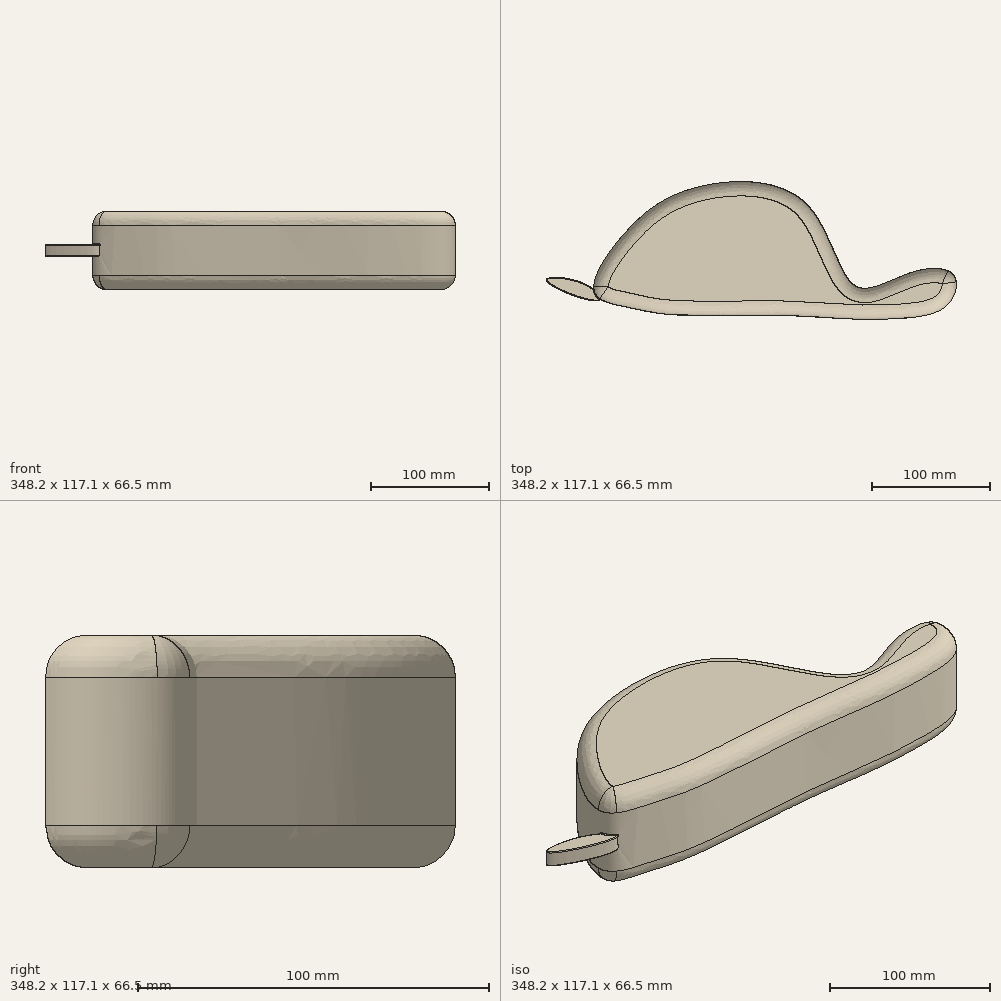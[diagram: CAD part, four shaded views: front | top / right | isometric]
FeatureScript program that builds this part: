
annotation { "Feature Type Name" : "Feature", "Feature Type Description" : "" }
export const myFeature = defineFeature(function(context is Context, id is Id, definition is map)
    precondition{}
    {
        {
            var Q0;
            Q0=qCreatedBy(makeId("Top.planeOp"),FACE);
            var sketch = newSketch(context, id + "F0", { "sketchPlane" : qUnion([Q0])});
            skFitSpline(sketch, "E0", {"points": [v(-149.95, -51.7) * mm, v(-123, 0) * mm, v(-63.14, 37.56) * mm, v(29.4, 23.95) * mm, v(71.85, -46.26) * mm, v(119.74, -34.56) * mm, v(155.12, -37.28) * mm, v(151.04, -61.23) * mm, v(114.84, -73.48) * mm, v(60.96, -74.02) * mm, v(8.98, -71.03) * mm, v(-86.54, -70.48) * mm, v(-122.46, -64.23) * mm, v(-149.95, -51.7) * mm]});
            skSolve(sketch);
        }
        {
            var Q0;
            Q0=makeQuery(id+"F0.imprint","IMPRINT",FACE,{"disambiguationData":[TD([[makeQuery(id+"F0.imprint","IMPRINT",EDGE,{"derivedFrom":sQuery(id+"F0.wireOp",EDGE,"E0")}),-1.0]])]});
            extrude(context, id + "F1", {"entities" : qUnion([Q0]), "depth" : 33.27 * mm});
        }
        {
            var Q0;
            Q0=makeQuery(id+"F1.opExtrude","CAP_FACE",FACE,{"disambiguationData":[OSD([sQuery(id+"F0.wireOp",EDGE,"E0")])],"isStart":true});
            extrude(context, id + "F2", {"entities" : qUnion([Q0]), "operationType" : NewBodyOperationType.ADD, "depth" : 33.27 * mm});
        }
        {
            var Q0;
            Q0=makeQuery(id+"F2.opExtrude","CAP_FACE",FACE,{"disambiguationData":[OSD([sQuery(id+"F0.wireOp",EDGE,"E0")])],"isStart":false});
            fillet(context, id + "F3", {"entities" : qUnion([Q0]), "radius" : 12.26 * mm, "tangentPropagation" : true, "allowEdgeOverflow" : false});
        }
        {
            var Q0;
            Q0=makeQuery(id+"F1.opExtrude","CAP_FACE",FACE,{"disambiguationData":[OSD([sQuery(id+"F0.wireOp",EDGE,"E0")])],"isStart":false});
            fillet(context, id + "F4", {"entities" : qUnion([Q0]), "radius" : 12.2 * mm, "tangentPropagation" : true, "allowEdgeOverflow" : false});
        }
        {
            var Q0;
            Q0=qCreatedBy(makeId("Top.planeOp"),FACE);
            var sketch = newSketch(context, id + "F5", { "sketchPlane" : qUnion([Q0])});
            skFitSpline(sketch, "E1", {"points": [v(-144.37, -57.1) * mm, v(-160.78, -56.76) * mm, v(-190.87, -41.03) * mm, v(-162.49, -42.74) * mm, v(-144.37, -57.1) * mm]});
            skSolve(sketch);
        }
        {
            var Q0;
            Q0=makeQuery(id+"F5.imprint","IMPRINT",FACE,{"disambiguationData":[TD([[makeQuery(id+"F5.imprint","IMPRINT",EDGE,{"derivedFrom":sQuery(id+"F5.wireOp",EDGE,"E1")}),-1.0]])]});
            extrude(context, id + "F6", {"entities" : qUnion([Q0]), "operationType" : NewBodyOperationType.ADD, "depth" : 5.08 * mm});
        }
        {
            var Q0;
            Q0=makeQuery(id+"F6.opExtrude","CAP_FACE",FACE,{"disambiguationData":[OSD([sQuery(id+"F5.wireOp",EDGE,"E1")])],"isStart":true});
            extrude(context, id + "F7", {"entities" : qUnion([Q0]), "operationType" : NewBodyOperationType.ADD, "depth" : 5.08 * mm});
        }
        {
            var Q0;
            Q0=makeQuery(id+"F6.opExtrude","CAP_FACE",FACE,{"disambiguationData":[OSD([sQuery(id+"F5.wireOp",EDGE,"E1")])],"isStart":false});
            fillet(context, id + "F8", {"entities" : qUnion([Q0]), "radius" : 0.61 * mm, "tangentPropagation" : true, "allowEdgeOverflow" : false});
        }
        {
            var Q0;
            Q0=makeQuery(id+"F7.opExtrude","CAP_EDGE",EDGE,{"disambiguationData":[OSD([sQuery(id+"F5.wireOp",EDGE,"E1")])],"isStart":false});
            fillet(context, id + "F9", {"entities" : qUnion([Q0]), "radius" : 0.6 * mm, "tangentPropagation" : true, "allowEdgeOverflow" : false});
        }
    });
